# Revit family: CoolBox i 160-400 315-1400
name_source: partatom
category: Оборудование
units: mm (PartAtom-declared; Revit-internal decimal feet)

## family parameters
Всегда вертикально = Да
Классификация = Нет
На основе рабочей плоскости = Нет
Общий = Нет
При загрузке вырезать с полостями = Нет
Размер круглого соединителя = Использовать диаметр
Тип детали = Нормальный
Точка расчета площади = Нет

## types (1)
- CoolBox i 160-400 315-1400
    A = 710 мм
    ADSK_Единица измерения = шт.
    ADSK_Завод-изготовитель = ООО «Турков»
    ADSK_Количество = 1
    ADSK_Марка = CoolBox i-315-1400-7.0
    ADSK_Наименование = Канальный охладитель Cool-Box испарительный блок
    ADSK_Холодильная мощность = 7000 Вт
    B = 656 мм
    C = 400 мм
    D = 315 мм
    Высота УГО = 531 мм
    Высота вв = 35 мм
    Г фреон от оси = 62 мм
    До оси вв = 250 мм
    Дренаж = 25 мм
    Дренаж от края = 46 мм
    Левый = Нет
    Правый = Да
    Соед г фреона = 417 мм
    УГО угол = 12.53°
    Фреон г = 15 мм
    Фреон ж = 10 мм
    Ширина УГО = 508 мм
    фитинг = 250 мм

## geometry (parser evidence)
native form markers: Blend x4
no freeform markers — native parametric forms only
